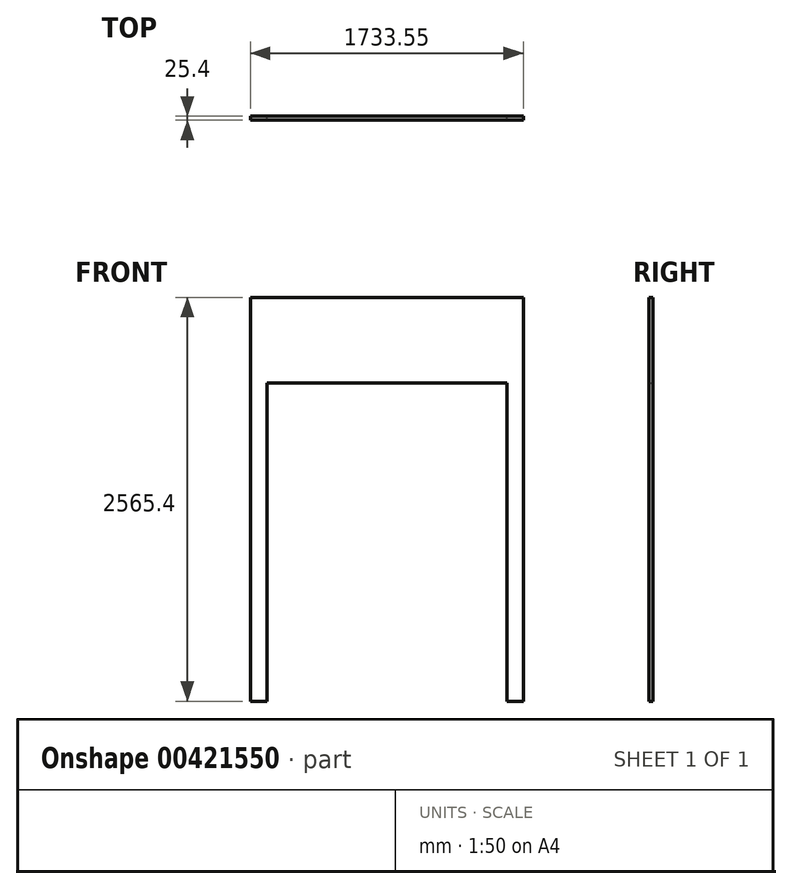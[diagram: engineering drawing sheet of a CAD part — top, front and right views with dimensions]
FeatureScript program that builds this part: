
annotation { "Feature Type Name" : "Feature", "Feature Type Description" : "" }
export const myFeature = defineFeature(function(context is Context, id is Id, definition is map)
    precondition{}
    {
        {
            var Q0;
            Q0=qCreatedBy(makeId("Front.planeOp"),FACE);
            var sketch = newSketch(context, id + "F0", { "sketchPlane" : qUnion([Q0])});
            skLineSegment(sketch, "E0.bottom", {"start": v(0, 0) * mm, "end": v(104.77, 0) * mm});
            skLineSegment(sketch, "E0.top", {"start": v(0, 2565.4) * mm, "end": v(1733.55, 2565.4) * mm});
            skLineSegment(sketch, "E0.left", {"start": v(0, 0) * mm, "end": v(0, 2565.4) * mm});
            skLineSegment(sketch, "E0.right", {"start": v(1733.55, 0) * mm, "end": v(1733.55, 2565.4) * mm});
            skLineSegment(sketch, "E1.top", {"start": v(104.77, 2022.47) * mm, "end": v(1628.77, 2022.48) * mm});
            skLineSegment(sketch, "E1.left", {"start": v(104.78, 0) * mm, "end": v(104.77, 2022.47) * mm});
            skLineSegment(sketch, "E1.right", {"start": v(1628.78, 0) * mm, "end": v(1628.77, 2022.48) * mm});
            skLineSegment(sketch, "E2.trimOffspring", {"start": v(1628.78, 0) * mm, "end": v(1733.55, 0) * mm});
            skSolve(sketch);
        }
        {
            var Q0;
            Q0 = qSketchRegion(id + "F0", true);
            extrude(context, id + "F1", {"entities" : qUnion([Q0]), "depth" : 25.4 * mm});
        }
    });
